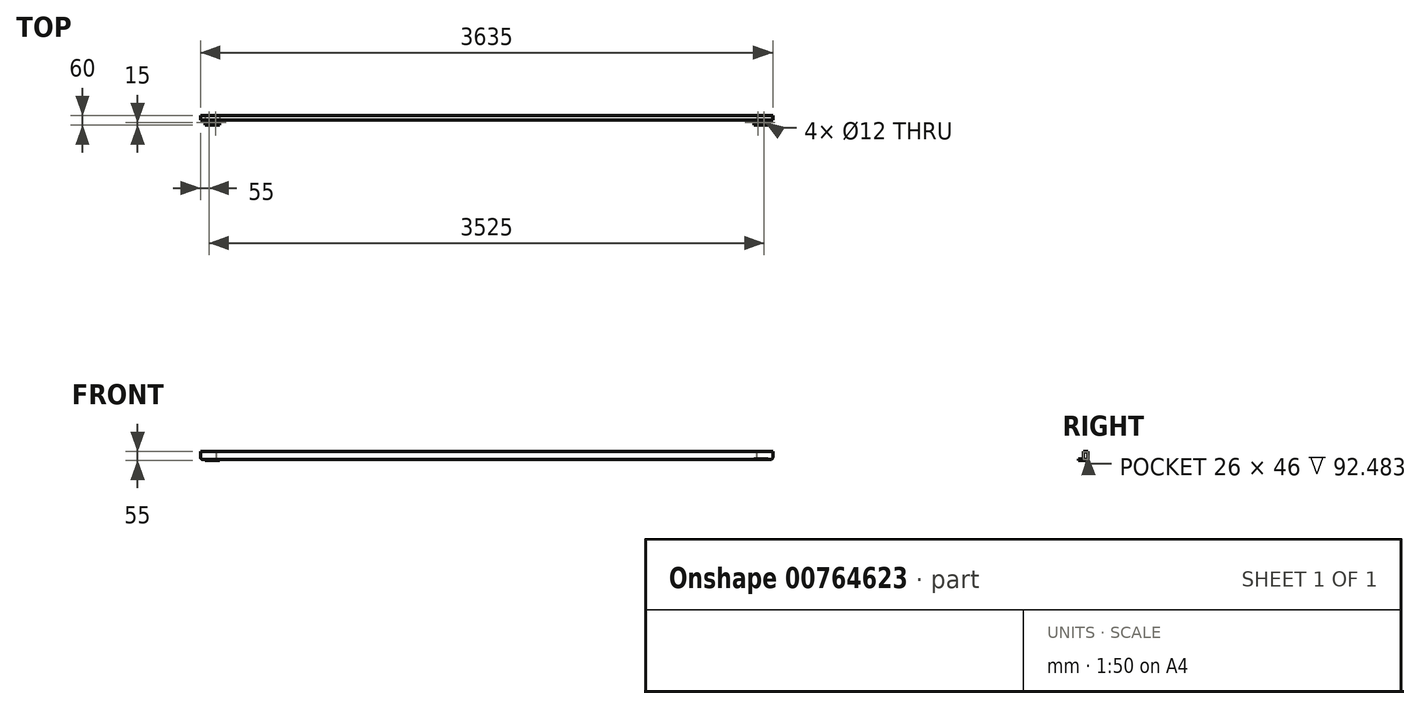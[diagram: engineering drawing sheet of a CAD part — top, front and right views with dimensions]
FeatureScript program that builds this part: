
annotation { "Feature Type Name" : "Feature", "Feature Type Description" : "" }
export const myFeature = defineFeature(function(context is Context, id is Id, definition is map)
    precondition{}
    {
        {
            var Q0;
            Q0=qCreatedBy(makeId("Front.planeOp"),FACE);
            var sketch = newSketch(context, id + "F0", { "sketchPlane" : qUnion([Q0])});
            skLineSegment(sketch, "E0.bottom", {"start": v(1787.5, -25) * mm, "end": v(-1787.5, -25) * mm});
            skLineSegment(sketch, "E0.top", {"start": v(1787.5, 25) * mm, "end": v(-1787.5, 25) * mm});
            skLineSegment(sketch, "E0.left", {"start": v(1787.5, -25) * mm, "end": v(1787.5, 25) * mm});
            skLineSegment(sketch, "E0.right", {"start": v(-1787.5, -25) * mm, "end": v(-1787.5, 25) * mm});
            skPoint(sketch, "E0.middle", {"position": v(0, 0) * mm});
            skSolve(sketch);
        }
        {
            var Q0;
            Q0=qSketchRegion(id+"F0",true);
            extrude(context, id + "F1", {"entities" : qUnion([Q0]), "depth" : 15 * mm, "offsetDistance" : 25 * mm, "hasSecondDirection" : true, "secondDirectionOppositeDirection" : true, "secondDirectionDepth" : 15 * mm});
        }
        {
            var Q0;
            Q0=makeQuery(id+"F1.opExtrude","SWEPT_FACE",FACE,{"disambiguationData":[OSD([sQuery(id+"F0.wireOp",EDGE,"E0.bottom")])]});
            var sketch = newSketch(context, id + "F2", { "sketchPlane" : qUnion([Q0])});
            skLineSegment(sketch, "E1.0", {"start": v(-1787.5, 15) * mm, "end": v(-1787.5, -15) * mm});
            skLineSegment(sketch, "E2.bottom", {"start": v(-1787.5, -15) * mm, "end": v(-1697.5, -15) * mm});
            skLineSegment(sketch, "E2.top", {"start": v(-1787.5, 45) * mm, "end": v(-1697.5, 45) * mm});
            skLineSegment(sketch, "E2.left", {"start": v(-1787.5, -15) * mm, "end": v(-1787.5, 45) * mm});
            skLineSegment(sketch, "E2.right", {"start": v(-1697.5, -15) * mm, "end": v(-1697.5, 45) * mm});
            skSolve(sketch);
        }
        {
            var Q0;
            Q0=qSketchRegion(id+"F2",true);
            extrude(context, id + "F3", {"entities" : qUnion([Q0]), "operationType" : NewBodyOperationType.ADD, "depth" : 5 * mm, "offsetDistance" : 25 * mm});
        }
        {
            var Q0;
            Q0=makeQuery(id+"F1.opExtrude","SWEPT_FACE",FACE,{"disambiguationData":[OSD([sQuery(id+"F0.wireOp",EDGE,"E0.bottom")])]});
            var sketch = newSketch(context, id + "F4", { "sketchPlane" : qUnion([Q0])});
            skLineSegment(sketch, "E3.0", {"start": v(1787.5, 15) * mm, "end": v(1787.5, -15) * mm});
            skLineSegment(sketch, "E4.bottom", {"start": v(1787.5, -15) * mm, "end": v(1697.5, -15) * mm});
            skLineSegment(sketch, "E4.top", {"start": v(1787.5, 45) * mm, "end": v(1697.5, 45) * mm});
            skLineSegment(sketch, "E4.left", {"start": v(1787.5, -15) * mm, "end": v(1787.5, 45) * mm});
            skLineSegment(sketch, "E4.right", {"start": v(1697.5, -15) * mm, "end": v(1697.5, 45) * mm});
            skSolve(sketch);
        }
        {
            var Q0;
            Q0=qSketchRegion(id+"F4",true);
            extrude(context, id + "F5", {"entities" : qUnion([Q0]), "operationType" : NewBodyOperationType.ADD, "depth" : 5 * mm, "offsetDistance" : 25 * mm});
        }
        {
            var Q0;
            Q0=makeQuery(id+"F3.opExtrude","CAP_FACE",FACE,{"disambiguationData":[OSD([sQuery(id+"F2.wireOp",EDGE,"E2.bottom"),sQuery(id+"F2.wireOp",EDGE,"E2.top"),sQuery(id+"F2.wireOp",EDGE,"E2.left"),sQuery(id+"F2.wireOp",EDGE,"E2.right")])],"isStart":false});
            var sketch = newSketch(context, id + "F6", { "sketchPlane" : qUnion([Q0])});
            skCircle(sketch, "E5.0", {"center": v(-935, 30) * mm, "radius": 6 * mm});
            skCircle(sketch, "E6.0", {"center": v(-975, 30) * mm, "radius": 6 * mm});
            skSolve(sketch);
        }
        {
            var Q0;
            Q0=qSketchRegion(id+"F6",true);
            var Q1;
            Q1=makeQuery(id+"F3.opExtrude","CAP_FACE",FACE,{"disambiguationData":[OSD([sQuery(id+"F2.wireOp",EDGE,"E2.bottom"),sQuery(id+"F2.wireOp",EDGE,"E2.top"),sQuery(id+"F2.wireOp",EDGE,"E2.left"),sQuery(id+"F2.wireOp",EDGE,"E2.right")])],"isStart":true});
            extrude(context, id + "F7", {"entities" : qUnion([Q0]), "operationType" : NewBodyOperationType.REMOVE, "endBound" : BoundingType.UP_TO_SURFACE, "oppositeDirection" : true, "depth" : 25 * mm, "endBoundEntityFace" : qUnion([Q1]), "offsetDistance" : 25 * mm});
        }
        {
            var Q0;
            Q0=makeQuery(id+"F5.opExtrude","CAP_FACE",FACE,{"disambiguationData":[OSD([sQuery(id+"F4.wireOp",EDGE,"E4.bottom"),sQuery(id+"F4.wireOp",EDGE,"E4.top"),sQuery(id+"F4.wireOp",EDGE,"E4.left"),sQuery(id+"F4.wireOp",EDGE,"E4.right")])],"isStart":false});
            var sketch = newSketch(context, id + "F8", { "sketchPlane" : qUnion([Q0])});
            skCircle(sketch, "E7.0", {"center": v(1762.5, 30) * mm, "radius": 6 * mm});
            skCircle(sketch, "E8.0", {"center": v(1722.5, 30) * mm, "radius": 6 * mm});
            skSolve(sketch);
        }
        {
            var Q0;
            Q0=qSketchRegion(id+"F8",true);
            var Q1;
            Q1=makeQuery(id+"F5.opExtrude","CAP_FACE",FACE,{"disambiguationData":[OSD([sQuery(id+"F4.wireOp",EDGE,"E4.bottom"),sQuery(id+"F4.wireOp",EDGE,"E4.top"),sQuery(id+"F4.wireOp",EDGE,"E4.left"),sQuery(id+"F4.wireOp",EDGE,"E4.right")])],"isStart":true});
            extrude(context, id + "F9", {"entities" : qUnion([Q0]), "operationType" : NewBodyOperationType.REMOVE, "endBound" : BoundingType.UP_TO_SURFACE, "oppositeDirection" : true, "depth" : 25 * mm, "endBoundEntityFace" : qUnion([Q1]), "offsetDistance" : 25 * mm});
        }
        {
            var Q0;
            Q0=makeQuery(id+"F1.opExtrude","SWEPT_FACE",FACE,{"disambiguationData":[OSD([sQuery(id+"F0.wireOp",EDGE,"E0.bottom")])]});
            var sketch = newSketch(context, id + "F10", { "sketchPlane" : qUnion([Q0])});
            skLineSegment(sketch, "E9", {"start": v(-1697.5, -15) * mm, "end": v(-1667.5, -15) * mm, "construction": true});
            skLineSegment(sketch, "E10", {"start": v(-1667.5, -15) * mm, "end": v(-1667.5, 15) * mm, "construction": true});
            skCircle(sketch, "E11", {"center": v(-1667.5, 0) * mm, "radius": 6 * mm});
            skLineSegment(sketch, "E12", {"start": v(1697.5, -15) * mm, "end": v(1667.5, -15) * mm, "construction": true});
            skLineSegment(sketch, "E13", {"start": v(1667.5, -15) * mm, "end": v(1667.5, 15) * mm, "construction": true});
            skCircle(sketch, "E14", {"center": v(1667.5, 0) * mm, "radius": 6 * mm});
            skLineSegment(sketch, "E15", {"start": v(1667.5, 0) * mm, "end": v(1191.07, 0) * mm});
            skLineSegment(sketch, "E16", {"start": v(1191.07, 0) * mm, "end": v(714.64, 0) * mm});
            skLineSegment(sketch, "E17", {"start": v(714.64, 0) * mm, "end": v(238.21, 0) * mm});
            skLineSegment(sketch, "E18", {"start": v(238.21, 0) * mm, "end": v(-238.21, 0) * mm});
            skLineSegment(sketch, "E19", {"start": v(-238.21, 0) * mm, "end": v(-714.64, 0) * mm});
            skLineSegment(sketch, "E20", {"start": v(-714.64, 0) * mm, "end": v(-1191.07, 0) * mm});
            skLineSegment(sketch, "E21", {"start": v(-1667.5, 0) * mm, "end": v(-1191.07, 0) * mm});
            skCircle(sketch, "E22", {"center": v(-1191.07, 0) * mm, "radius": 6 * mm});
            skCircle(sketch, "E23", {"center": v(-714.64, 0) * mm, "radius": 6 * mm});
            skCircle(sketch, "E24", {"center": v(-238.21, 0) * mm, "radius": 6 * mm});
            skCircle(sketch, "E25", {"center": v(238.21, 0) * mm, "radius": 6 * mm});
            skCircle(sketch, "E26", {"center": v(714.64, 0) * mm, "radius": 6 * mm});
            skCircle(sketch, "E27", {"center": v(1191.07, 0) * mm, "radius": 6 * mm});
            skSolve(sketch);
        }
        {
            var Q0;
            Q0=makeQuery(id+"F3.opExtrude","CAP_FACE",FACE,{"disambiguationData":[OSD([sQuery(id+"F2.wireOp",EDGE,"E2.bottom"),sQuery(id+"F2.wireOp",EDGE,"E2.top"),sQuery(id+"F2.wireOp",EDGE,"E2.left"),sQuery(id+"F2.wireOp",EDGE,"E2.right")])],"isStart":false});
            var sketch = newSketch(context, id + "F11", { "sketchPlane" : qUnion([Q0])});
            skLineSegment(sketch, "E28.bottom", {"start": v(-1787.5, 45) * mm, "end": v(-1762.5, 45) * mm, "construction": true});
            skLineSegment(sketch, "E28.top", {"start": v(-1787.5, 30) * mm, "end": v(-1762.5, 30) * mm});
            skLineSegment(sketch, "E28.left", {"start": v(-1787.5, 45) * mm, "end": v(-1787.5, 30) * mm});
            skLineSegment(sketch, "E28.right", {"start": v(-1762.5, 45) * mm, "end": v(-1762.5, 30) * mm});
            skLineSegment(sketch, "E29", {"start": v(-1762.5, 30) * mm, "end": v(-1722.5, 30) * mm});
            skCircle(sketch, "E30", {"center": v(-1762.5, 30) * mm, "radius": 6 * mm});
            skCircle(sketch, "E31", {"center": v(-1722.5, 30) * mm, "radius": 6 * mm});
            skSolve(sketch);
        }
        {
            var Q0;
            Q0=qSketchRegion(id+"F11",true);
            extrude(context, id + "F12", {"entities" : qUnion([Q0]), "operationType" : NewBodyOperationType.REMOVE, "endBound" : BoundingType.UP_TO_NEXT, "oppositeDirection" : true, "depth" : 25 * mm, "offsetDistance" : 25 * mm});
        }
        {
            var Q0;
            Q0=makeQuery(id+"F5.boolean.opBoolean","MERGE",FACE,{"derivedFrom":[makeQuery(id+"F1.opExtrude","SWEPT_FACE",FACE,{"disambiguationData":[OSD([sQuery(id+"F0.wireOp",EDGE,"E0.left")])]}),makeQuery(id+"F5.opExtrude","SWEPT_FACE",FACE,{"disambiguationData":[OSD([sQuery(id+"F4.wireOp",EDGE,"E4.left")])]})]});
            var sketch = newSketch(context, id + "F13", { "sketchPlane" : qUnion([Q0])});
            skLineSegment(sketch, "E32.bottom", {"start": v(-15, 25) * mm, "end": v(15, 25) * mm});
            skLineSegment(sketch, "E32.top", {"start": v(-15, -25) * mm, "end": v(15, -25) * mm});
            skLineSegment(sketch, "E32.left", {"start": v(-15, 25) * mm, "end": v(-15, -25) * mm});
            skLineSegment(sketch, "E32.right", {"start": v(15, 25) * mm, "end": v(15, -25) * mm});
            skSolve(sketch);
        }
        {
            var Q0;
            Q0=qSketchRegion(id+"F13",true);
            extrude(context, id + "F14", {"entities" : qUnion([Q0]), "operationType" : NewBodyOperationType.ADD, "depth" : 30 * mm, "offsetDistance" : 25 * mm});
        }
        {
            var Q0;
            Q0=makeQuery(id+"F14.opExtrude","CAP_EDGE",EDGE,{"disambiguationData":[OSD([sQuery(id+"F13.wireOp",EDGE,"E32.top")])],"isStart":false});
            fillet(context, id + "F15", {"entities" : qUnion([Q0]), "radius" : 15 * mm, "tangentPropagation" : true, "allowEdgeOverflow" : false});
        }
        {
            var Q0;
            Q0=makeQuery(id+"F14.opExtrude","CAP_FACE",FACE,{"disambiguationData":[OSD([sQuery(id+"F13.wireOp",EDGE,"E32.bottom"),sQuery(id+"F13.wireOp",EDGE,"E32.top"),sQuery(id+"F13.wireOp",EDGE,"E32.left"),sQuery(id+"F13.wireOp",EDGE,"E32.right")])],"isStart":false});
            var sketch = newSketch(context, id + "F16", { "sketchPlane" : qUnion([Q0])});
            skLineSegment(sketch, "E33.bottom", {"start": v(-15, 25) * mm, "end": v(15, 25) * mm});
            skLineSegment(sketch, "E33.top", {"start": v(-15, -25) * mm, "end": v(15, -25) * mm});
            skLineSegment(sketch, "E33.left", {"start": v(-15, 25) * mm, "end": v(-15, -25) * mm});
            skLineSegment(sketch, "E33.right", {"start": v(15, 25) * mm, "end": v(15, -25) * mm});
            skLineSegment(sketch, "E34", {"start": v(-15, -25) * mm, "end": v(15, 25) * mm, "construction": true});
            skLineSegment(sketch, "E35.bottom", {"start": v(13, -23) * mm, "end": v(-13, -23) * mm});
            skLineSegment(sketch, "E35.top", {"start": v(13, 23) * mm, "end": v(-13, 23) * mm});
            skLineSegment(sketch, "E35.left", {"start": v(13, -23) * mm, "end": v(13, 23) * mm});
            skLineSegment(sketch, "E35.right", {"start": v(-13, -23) * mm, "end": v(-13, 23) * mm});
            skPoint(sketch, "E35.middle", {"position": v(0, 0) * mm});
            skSolve(sketch);
        }
        {
            var Q0;
            {var subQ0=sQuery(id+"F16.wireOp",EDGE,"E35.bottom");Q0=makeQuery(id+"F16.imprint","IMPRINT",FACE,{"disambiguationData":[TD([[makeQuery(id+"F16.imprint","IMPRINT",EDGE,{"derivedFrom":subQ0}),-1.0]])]});}
            var Q1;
            {var subQ0=sQuery(id+"F16.wireOp",EDGE,"E35.top");Q1=makeQuery(id+"F16.imprint","IMPRINT",FACE,{"disambiguationData":[TD([[makeQuery(id+"F16.imprint","IMPRINT",EDGE,{"derivedFrom":subQ0}),1.0]])]});}
            extrude(context, id + "F17", {"entities" : qUnion([Q0, Q1]), "operationType" : NewBodyOperationType.REMOVE, "oppositeDirection" : true, "depth" : 100 * mm, "offsetDistance" : 25 * mm});
        }
        {
            var Q0;
            Q0=makeQuery(id+"F3.boolean.opBoolean","MERGE",FACE,{"derivedFrom":[makeQuery(id+"F1.opExtrude","SWEPT_FACE",FACE,{"disambiguationData":[OSD([sQuery(id+"F0.wireOp",EDGE,"E0.right")])]}),makeQuery(id+"F3.opExtrude","SWEPT_FACE",FACE,{"disambiguationData":[OSD([sQuery(id+"F2.wireOp",EDGE,"E2.left")])]})]});
            var sketch = newSketch(context, id + "F18", { "sketchPlane" : qUnion([Q0])});
            skLineSegment(sketch, "E36.bottom", {"start": v(-15, 25) * mm, "end": v(15, 25) * mm});
            skLineSegment(sketch, "E36.top", {"start": v(-15, -25) * mm, "end": v(15, -25) * mm});
            skLineSegment(sketch, "E36.left", {"start": v(-15, 25) * mm, "end": v(-15, -25) * mm});
            skLineSegment(sketch, "E36.right", {"start": v(15, 25) * mm, "end": v(15, -25) * mm});
            skSolve(sketch);
        }
        {
            var Q0;
            Q0=qSketchRegion(id+"F18",true);
            extrude(context, id + "F19", {"entities" : qUnion([Q0]), "operationType" : NewBodyOperationType.ADD, "depth" : 30 * mm, "offsetDistance" : 25 * mm});
        }
        {
            var Q0;
            Q0=makeQuery(id+"F19.opExtrude","CAP_FACE",FACE,{"disambiguationData":[OSD([sQuery(id+"F18.wireOp",EDGE,"E36.bottom"),sQuery(id+"F18.wireOp",EDGE,"E36.top"),sQuery(id+"F18.wireOp",EDGE,"E36.left"),sQuery(id+"F18.wireOp",EDGE,"E36.right")])],"isStart":false});
            var sketch = newSketch(context, id + "F20", { "sketchPlane" : qUnion([Q0])});
            skLineSegment(sketch, "E37.bottom", {"start": v(-15, 25) * mm, "end": v(15, 25) * mm});
            skLineSegment(sketch, "E37.top", {"start": v(-15, -25) * mm, "end": v(15, -25) * mm});
            skLineSegment(sketch, "E37.left", {"start": v(-15, 25) * mm, "end": v(-15, -25) * mm});
            skLineSegment(sketch, "E37.right", {"start": v(15, 25) * mm, "end": v(15, -25) * mm});
            skLineSegment(sketch, "E38", {"start": v(15, -25) * mm, "end": v(-15, 25) * mm, "construction": true});
            skLineSegment(sketch, "E39.bottom", {"start": v(13, 23) * mm, "end": v(-13, 23) * mm});
            skLineSegment(sketch, "E39.top", {"start": v(13, -23) * mm, "end": v(-13, -23) * mm});
            skLineSegment(sketch, "E39.left", {"start": v(13, 23) * mm, "end": v(13, -23) * mm});
            skLineSegment(sketch, "E39.right", {"start": v(-13, 23) * mm, "end": v(-13, -23) * mm});
            skPoint(sketch, "E39.middle", {"position": v(0, 0) * mm});
            skSolve(sketch);
        }
        {
            var Q0;
            Q0=makeQuery(id+"F20.imprint","IMPRINT",FACE,{"disambiguationData":[TD([[makeQuery(id+"F20.imprint","IMPRINT",EDGE,{"derivedFrom":sQuery(id+"F20.wireOp",EDGE,"E39.bottom")}),1.0]])]});
            extrude(context, id + "F21", {"entities" : qUnion([Q0]), "operationType" : NewBodyOperationType.REMOVE, "oppositeDirection" : true, "depth" : 100 * mm, "offsetDistance" : 25 * mm});
        }
        {
            var Q0;
            Q0=makeQuery(id+"F19.opExtrude","CAP_EDGE",EDGE,{"disambiguationData":[OSD([sQuery(id+"F18.wireOp",EDGE,"E36.top")])],"isStart":false});
            fillet(context, id + "F22", {"entities" : qUnion([Q0]), "radius" : 15 * mm, "tangentPropagation" : true, "allowEdgeOverflow" : false});
        }
        {
            var Q0;
            Q0=makeQuery(id+"F5.opExtrude","CAP_FACE",FACE,{"disambiguationData":[OSD([sQuery(id+"F4.wireOp",EDGE,"E4.bottom"),sQuery(id+"F4.wireOp",EDGE,"E4.top"),sQuery(id+"F4.wireOp",EDGE,"E4.left"),sQuery(id+"F4.wireOp",EDGE,"E4.right")])],"isStart":true});
            extrude(context, id + "F23", {"entities" : qUnion([Q0]), "operationType" : NewBodyOperationType.ADD, "depth" : 5 * mm, "offsetDistance" : 25 * mm});
        }
        {
            var Q0;
            Q0=makeQuery(id+"F5.opExtrude","CAP_FACE",FACE,{"disambiguationData":[OSD([sQuery(id+"F4.wireOp",EDGE,"E4.bottom"),sQuery(id+"F4.wireOp",EDGE,"E4.top"),sQuery(id+"F4.wireOp",EDGE,"E4.left"),sQuery(id+"F4.wireOp",EDGE,"E4.right")])],"isStart":false});
            extrude(context, id + "F24", {"entities" : qUnion([Q0]), "operationType" : NewBodyOperationType.REMOVE, "oppositeDirection" : true, "depth" : 5 * mm, "offsetDistance" : 25 * mm});
        }
    });
